# Revit family: Casement_36_B_Side_Hung_Standard
name_source: partatom
category: Windows
revit_build: Autodesk Revit 2014 (Build: 20130308_1515(x64)
units: mm (PartAtom-declared; Revit-internal decimal feet)

## types (18) — shared parameters
Aluminium Thickness = 1 mm  [stored 0.00328084 ft]
Bead SG Gap = 13 mm  [stored 0.0426509 ft]
Casement Dimension = 36 mm  [stored 0.11811 ft]
Custom Sash Width = 554 mm  [stored 1.81759 ft]
DG Extrusion Start = 8 mm  [stored 0.0262467 ft]
DG Gasket Finish = Double Glazing Gasket Material
DG Thickness Calc = 4 mm  [stored 0.0131234 ft]
Default Sill Height = 800 mm  [stored 2.62467 ft]
Depth Bead = 22 mm  [stored 0.0721785 ft]
Depth Mullion = 37 mm  [stored 0.121391 ft]
Description = Window 36mm, Type B side hung
Frame Center Offset = 18 mm  [stored 0.0590551 ft]
Limit Fixed Panel Width Max = 1500 mm
Limit Fixed Panel Width Min = 200 mm  [stored 0.656168 ft]
Limit Sash Height Max = 1300 mm  [stored 4.26509 ft]
Limit Sash Height Min = 300 mm  [stored 0.984252 ft]
Limit Sash Width Max = 600 mm  [stored 1.9685 ft]
Limit Sash Width Min = 300 mm  [stored 0.984252 ft]
Limit Window Height Max = 1346 mm  [stored 4.41601 ft]
Limit Window Height Min = 346 mm
Limit Window Width Max = 2129 mm
Limit Window Width Min = 829 mm  [stored 2.71982 ft]
Manufacturer = Crealco
Max System DG One Piece Thickness = 6 mm  [stored 0.019685 ft]
Max System DG Unit Thickness = 25 mm  [stored 0.082021 ft]
Model = Casement 36
Mullion Depth Windload Based = 37 mm  [stored 0.121391 ft]
Offset Bead SG Center Reversed = 18 mm  [stored 0.0590551 ft]
Offset Mullion Left = 569 mm  [stored 1.8668 ft]
Offset Panel 4 Left = 599 mm  [stored 1.96522 ft]
Offset Sash Left = 23 mm  [stored 0.0754593 ft]
Offset Sash Top = 23 mm  [stored 0.0754593 ft]
Offset Window Exterior = 18 mm  [stored 0.0590551 ft]
SG Gasket Thickness = 6 mm  [stored 0.019685 ft]
Sash Center Offset = 15 mm  [stored 0.0492126 ft]
Sash Overlap = 7 mm  [stored 0.0229659 ft]
Sash Spacing Inner = 8 mm  [stored 0.0262467 ft]
URL = http://www.crealco.co.za
Wall Closure = By host
Width Bead = 15 mm  [stored 0.0492126 ft]
Width Panel 1 = 539 mm  [stored 1.76837 ft]
Width Profile = 30 mm  [stored 0.0984252 ft]
Width Sash = 524 mm  [stored 1.71916 ft]
Width Sash Opening = 554 mm  [stored 1.81759 ft]
zero-valued in all types: Window Exterior Offset

## per-type parameters (varying)
- 36-0909S-1000Pa: Area Pane Left=0.37 m²; Area Pane Right=0.21 m²; Clearvue Insulated LowE SHGC Value=0.451; Clearvue Insulated LowE U Value=3.84; Clearvue Insulated SHGC Value=0.495; Clearvue Insulated U Value=4.31; Clearvue U Value=6.23; Custom Windload=1000 mm  [stored 3.28084 ft]; Custom Window Height=890 mm  [stored 2.91995 ft]; Custom Window Width=890 mm  [stored 2.91995 ft]; Energy Advantage SHGC Value=0.503; Energy Advantage U Value=4.91; Height=890 mm  [stored 2.91995 ft]; Height Panel 4=830 mm  [stored 2.7231 ft]; Height Sash=814 mm  [stored 2.6706 ft]; Height Sash Opening=844 mm  [stored 2.76903 ft]; Intruderprufe Insulated LowE SHGC Value=0.416; Intruderprufe Insulated LowE U Value=3.76; Intruderprufe Insulated SHGC Value=0.452; Intruderprufe Insulated U Value=4.19; Intruderprufe LowE SHGC Value=0.474; Intruderprufe LowE U Value=4.8; Intruderprufe SHGC Value=0.535; Intruderprufe U Value=6.09; Length Mullion=890 mm  [stored 2.91995 ft]; Max Pane Area=0.37 m²; Width=890 mm  [stored 2.91995 ft]; Width Panel 4=261 mm  [stored 0.856299 ft]; Windload Design=1000 mm  [stored 3.28084 ft]
- 36-1209S-1000Pa: Area Pane Left=0.37 m²; Area Pane Right=0.45 m²; Clearvue Insulated LowE SHGC Value=0.49; Clearvue Insulated LowE U Value=3.52; Clearvue Insulated SHGC Value=0.538; Clearvue Insulated U Value=4.04; Clearvue U Value=6.16; Custom Windload=1000 mm  [stored 3.28084 ft]; Custom Window Height=890 mm  [stored 2.91995 ft]; Custom Window Width=1190 mm  [stored 3.9042 ft]; Energy Advantage SHGC Value=0.546; Energy Advantage U Value=4.7; Height=890 mm  [stored 2.91995 ft]; Height Panel 4=830 mm  [stored 2.7231 ft]; Height Sash=814 mm  [stored 2.6706 ft]; Height Sash Opening=844 mm  [stored 2.76903 ft]; Intruderprufe Insulated LowE SHGC Value=0.451; Intruderprufe Insulated LowE U Value=3.44; Intruderprufe Insulated SHGC Value=0.492; Intruderprufe Insulated U Value=3.93; Intruderprufe LowE SHGC Value=0.513; Intruderprufe LowE U Value=4.59; Intruderprufe SHGC Value=0.581; Intruderprufe U Value=6.03; Length Mullion=890 mm  [stored 2.91995 ft]; Max Pane Area=0.45 m²; Width=1190 mm  [stored 3.9042 ft]; Width Panel 4=561 mm; Windload Design=1000 mm  [stored 3.28084 ft]
- 36-1509S-1000Pa: Area Pane Left=0.37 m²; Area Pane Right=0.7 m²; Clearvue Insulated LowE SHGC Value=0.513; Clearvue Insulated LowE U Value=3.32; Clearvue Insulated SHGC Value=0.563; Clearvue Insulated U Value=3.87; Clearvue U Value=6.12; Custom Windload=1000 mm  [stored 3.28084 ft]; Custom Window Height=890 mm  [stored 2.91995 ft]; Custom Window Width=1490 mm; Energy Advantage SHGC Value=0.572; Energy Advantage U Value=4.58; Height=890 mm  [stored 2.91995 ft]; Height Panel 4=830 mm  [stored 2.7231 ft]; Height Sash=814 mm  [stored 2.6706 ft]; Height Sash Opening=844 mm  [stored 2.76903 ft]; Intruderprufe Insulated LowE SHGC Value=0.472; Intruderprufe Insulated LowE U Value=3.25; Intruderprufe Insulated SHGC Value=0.516; Intruderprufe Insulated U Value=3.78; Intruderprufe LowE SHGC Value=0.537; Intruderprufe LowE U Value=4.47; Intruderprufe SHGC Value=0.609; Intruderprufe U Value=5.99; Length Mullion=890 mm  [stored 2.91995 ft]; Max Pane Area=0.7 m²; Width=1490 mm; Width Panel 4=861 mm  [stored 2.8248 ft]; Windload Design=1000 mm  [stored 3.28084 ft]
- 36-0912S-1000Pa: Area Pane Left=0.52 m²; Area Pane Right=0.28 m²; Clearvue Insulated LowE SHGC Value=0.469; Clearvue Insulated LowE U Value=3.71; Clearvue Insulated SHGC Value=0.515; Clearvue Insulated U Value=4.19; Clearvue U Value=6.21; Custom Windload=1000 mm  [stored 3.28084 ft]; Custom Window Height=1190 mm  [stored 3.9042 ft]; Custom Window Width=890 mm  [stored 2.91995 ft]; Energy Advantage SHGC Value=0.523; Energy Advantage U Value=4.82; Height=1190 mm  [stored 3.9042 ft]; Height Panel 4=1130 mm  [stored 3.70735 ft]; Height Sash=1114 mm  [stored 3.65486 ft]; Height Sash Opening=1144 mm; Intruderprufe Insulated LowE SHGC Value=0.432; Intruderprufe Insulated LowE U Value=3.62; Intruderprufe Insulated SHGC Value=0.471; Intruderprufe Insulated U Value=4.08; Intruderprufe LowE SHGC Value=0.493; Intruderprufe LowE U Value=4.71; Intruderprufe SHGC Value=0.556; Intruderprufe U Value=6.07; Length Mullion=1190 mm  [stored 3.9042 ft]; Max Pane Area=0.52 m²; Width=890 mm  [stored 2.91995 ft]; Width Panel 4=261 mm  [stored 0.856299 ft]; Windload Design=1000 mm  [stored 3.28084 ft]
- 36-1212S-1000Pa: Area Pane Left=0.52 m²; Area Pane Right=0.62 m²; Clearvue Insulated LowE SHGC Value=0.508; Clearvue Insulated LowE U Value=3.37; Clearvue Insulated SHGC Value=0.558; Clearvue Insulated U Value=3.92; Clearvue U Value=6.14; Custom Windload=1000 mm  [stored 3.28084 ft]; Custom Window Height=1190 mm  [stored 3.9042 ft]; Custom Window Width=1190 mm  [stored 3.9042 ft]; Energy Advantage SHGC Value=0.567; Energy Advantage U Value=4.61; Height=1190 mm  [stored 3.9042 ft]; Height Panel 4=1130 mm  [stored 3.70735 ft]; Height Sash=1114 mm  [stored 3.65486 ft]; Height Sash Opening=1144 mm; Intruderprufe Insulated LowE SHGC Value=0.469; Intruderprufe Insulated LowE U Value=3.3; Intruderprufe Insulated SHGC Value=0.511; Intruderprufe Insulated U Value=3.82; Intruderprufe LowE SHGC Value=0.532; Intruderprufe LowE U Value=4.51; Intruderprufe SHGC Value=0.603; Intruderprufe U Value=6; Length Mullion=1190 mm  [stored 3.9042 ft]; Max Pane Area=0.62 m²; Width=1190 mm  [stored 3.9042 ft]; Width Panel 4=561 mm; Windload Design=1000 mm  [stored 3.28084 ft]
- 36-1512S-1000Pa: Area Pane Left=0.52 m²; Area Pane Right=0.95 m²; Clearvue Insulated LowE SHGC Value=0.531; Clearvue Insulated LowE U Value=3.17; Clearvue Insulated SHGC Value=0.584; Clearvue Insulated U Value=3.75; Clearvue U Value=6.1; Custom Windload=1000 mm  [stored 3.28084 ft]; Custom Window Height=1190 mm  [stored 3.9042 ft]; Custom Window Width=1490 mm; Energy Advantage SHGC Value=0.593; Energy Advantage U Value=4.49; Height=1190 mm  [stored 3.9042 ft]; Height Panel 4=1130 mm  [stored 3.70735 ft]; Height Sash=1114 mm  [stored 3.65486 ft]; Height Sash Opening=1144 mm; Intruderprufe Insulated LowE SHGC Value=0.489; Intruderprufe Insulated LowE U Value=3.1; Intruderprufe Insulated SHGC Value=0.536; Intruderprufe Insulated U Value=3.66; Intruderprufe LowE SHGC Value=0.556; Intruderprufe LowE U Value=4.38; Intruderprufe SHGC Value=0.63; Intruderprufe U Value=5.96; Length Mullion=1190 mm  [stored 3.9042 ft]; Max Pane Area=0.95 m²; Width=1490 mm; Width Panel 4=861 mm  [stored 2.8248 ft]; Windload Design=1000 mm  [stored 3.28084 ft]
- 36-0909S-1500Pa: Area Pane Left=0.37 m²; Area Pane Right=0.21 m²; Clearvue Insulated LowE SHGC Value=0.451; Clearvue Insulated LowE U Value=3.84; Clearvue Insulated SHGC Value=0.495; Clearvue Insulated U Value=4.31; Clearvue U Value=6.23; Custom Windload=1500 mm; Custom Window Height=890 mm  [stored 2.91995 ft]; Custom Window Width=890 mm  [stored 2.91995 ft]; Energy Advantage SHGC Value=0.503; Energy Advantage U Value=4.91; Height=890 mm  [stored 2.91995 ft]; Height Panel 4=830 mm  [stored 2.7231 ft]; Height Sash=814 mm  [stored 2.6706 ft]; Height Sash Opening=844 mm  [stored 2.76903 ft]; Intruderprufe Insulated LowE SHGC Value=0.416; Intruderprufe Insulated LowE U Value=3.76; Intruderprufe Insulated SHGC Value=0.452; Intruderprufe Insulated U Value=4.19; Intruderprufe LowE SHGC Value=0.474; Intruderprufe LowE U Value=4.8; Intruderprufe SHGC Value=0.535; Intruderprufe U Value=6.09; Length Mullion=890 mm  [stored 2.91995 ft]; Max Pane Area=0.37 m²; Width=890 mm  [stored 2.91995 ft]; Width Panel 4=261 mm  [stored 0.856299 ft]; Windload Design=1500 mm
- 36-0909S-2000Pa: Area Pane Left=0.37 m²; Area Pane Right=0.21 m²; Clearvue Insulated LowE SHGC Value=0.451; Clearvue Insulated LowE U Value=3.84; Clearvue Insulated SHGC Value=0.495; Clearvue Insulated U Value=4.31; Clearvue U Value=6.23; Custom Windload=2000 mm; Custom Window Height=890 mm  [stored 2.91995 ft]; Custom Window Width=890 mm  [stored 2.91995 ft]; Energy Advantage SHGC Value=0.503; Energy Advantage U Value=4.91; Height=890 mm  [stored 2.91995 ft]; Height Panel 4=830 mm  [stored 2.7231 ft]; Height Sash=814 mm  [stored 2.6706 ft]; Height Sash Opening=844 mm  [stored 2.76903 ft]; Intruderprufe Insulated LowE SHGC Value=0.416; Intruderprufe Insulated LowE U Value=3.76; Intruderprufe Insulated SHGC Value=0.452; Intruderprufe Insulated U Value=4.19; Intruderprufe LowE SHGC Value=0.474; Intruderprufe LowE U Value=4.8; Intruderprufe SHGC Value=0.535; Intruderprufe U Value=6.09; Length Mullion=890 mm  [stored 2.91995 ft]; Max Pane Area=0.37 m²; Width=890 mm  [stored 2.91995 ft]; Width Panel 4=261 mm  [stored 0.856299 ft]; Windload Design=2000 mm
- 36-1209S-1500Pa: Area Pane Left=0.37 m²; Area Pane Right=0.45 m²; Clearvue Insulated LowE SHGC Value=0.49; Clearvue Insulated LowE U Value=3.52; Clearvue Insulated SHGC Value=0.538; Clearvue Insulated U Value=4.04; Clearvue U Value=6.16; Custom Windload=1500 mm; Custom Window Height=890 mm  [stored 2.91995 ft]; Custom Window Width=1190 mm  [stored 3.9042 ft]; Energy Advantage SHGC Value=0.546; Energy Advantage U Value=4.7; Height=890 mm  [stored 2.91995 ft]; Height Panel 4=830 mm  [stored 2.7231 ft]; Height Sash=814 mm  [stored 2.6706 ft]; Height Sash Opening=844 mm  [stored 2.76903 ft]; Intruderprufe Insulated LowE SHGC Value=0.451; Intruderprufe Insulated LowE U Value=3.44; Intruderprufe Insulated SHGC Value=0.492; Intruderprufe Insulated U Value=3.93; Intruderprufe LowE SHGC Value=0.513; Intruderprufe LowE U Value=4.59; Intruderprufe SHGC Value=0.581; Intruderprufe U Value=6.03; Length Mullion=890 mm  [stored 2.91995 ft]; Max Pane Area=0.45 m²; Width=1190 mm  [stored 3.9042 ft]; Width Panel 4=561 mm; Windload Design=1500 mm
- 36-1209S-2000Pa: Area Pane Left=0.37 m²; Area Pane Right=0.45 m²; Clearvue Insulated LowE SHGC Value=0.49; Clearvue Insulated LowE U Value=3.52; Clearvue Insulated SHGC Value=0.538; Clearvue Insulated U Value=4.04; Clearvue U Value=6.16; Custom Windload=2000 mm; Custom Window Height=890 mm  [stored 2.91995 ft]; Custom Window Width=1190 mm  [stored 3.9042 ft]; Energy Advantage SHGC Value=0.546; Energy Advantage U Value=4.7; Height=890 mm  [stored 2.91995 ft]; Height Panel 4=830 mm  [stored 2.7231 ft]; Height Sash=814 mm  [stored 2.6706 ft]; Height Sash Opening=844 mm  [stored 2.76903 ft]; Intruderprufe Insulated LowE SHGC Value=0.451; Intruderprufe Insulated LowE U Value=3.44; Intruderprufe Insulated SHGC Value=0.492; Intruderprufe Insulated U Value=3.93; Intruderprufe LowE SHGC Value=0.513; Intruderprufe LowE U Value=4.59; Intruderprufe SHGC Value=0.581; Intruderprufe U Value=6.03; Length Mullion=890 mm  [stored 2.91995 ft]; Max Pane Area=0.45 m²; Width=1190 mm  [stored 3.9042 ft]; Width Panel 4=561 mm; Windload Design=2000 mm
- 36-1509S-1500Pa: Area Pane Left=0.37 m²; Area Pane Right=0.7 m²; Clearvue Insulated LowE SHGC Value=0.513; Clearvue Insulated LowE U Value=3.32; Clearvue Insulated SHGC Value=0.563; Clearvue Insulated U Value=3.87; Clearvue U Value=6.12; Custom Windload=1500 mm; Custom Window Height=890 mm  [stored 2.91995 ft]; Custom Window Width=1490 mm; Energy Advantage SHGC Value=0.572; Energy Advantage U Value=4.58; Height=890 mm  [stored 2.91995 ft]; Height Panel 4=830 mm  [stored 2.7231 ft]; Height Sash=814 mm  [stored 2.6706 ft]; Height Sash Opening=844 mm  [stored 2.76903 ft]; Intruderprufe Insulated LowE SHGC Value=0.472; Intruderprufe Insulated LowE U Value=3.25; Intruderprufe Insulated SHGC Value=0.516; Intruderprufe Insulated U Value=3.78; Intruderprufe LowE SHGC Value=0.537; Intruderprufe LowE U Value=4.47; Intruderprufe SHGC Value=0.609; Intruderprufe U Value=5.99; Length Mullion=890 mm  [stored 2.91995 ft]; Max Pane Area=0.7 m²; Width=1490 mm; Width Panel 4=861 mm  [stored 2.8248 ft]; Windload Design=1500 mm
- 36-1509S-2000Pa: Area Pane Left=0.37 m²; Area Pane Right=0.7 m²; Clearvue Insulated LowE SHGC Value=0.513; Clearvue Insulated LowE U Value=3.32; Clearvue Insulated SHGC Value=0.563; Clearvue Insulated U Value=3.87; Clearvue U Value=6.12; Custom Windload=2000 mm; Custom Window Height=890 mm  [stored 2.91995 ft]; Custom Window Width=1490 mm; Energy Advantage SHGC Value=0.572; Energy Advantage U Value=4.58; Height=890 mm  [stored 2.91995 ft]; Height Panel 4=830 mm  [stored 2.7231 ft]; Height Sash=814 mm  [stored 2.6706 ft]; Height Sash Opening=844 mm  [stored 2.76903 ft]; Intruderprufe Insulated LowE SHGC Value=0.472; Intruderprufe Insulated LowE U Value=3.25; Intruderprufe Insulated SHGC Value=0.516; Intruderprufe Insulated U Value=3.78; Intruderprufe LowE SHGC Value=0.537; Intruderprufe LowE U Value=4.47; Intruderprufe SHGC Value=0.609; Intruderprufe U Value=5.99; Length Mullion=890 mm  [stored 2.91995 ft]; Max Pane Area=0.7 m²; Width=1490 mm; Width Panel 4=861 mm  [stored 2.8248 ft]; Windload Design=2000 mm
- 36-0912S-1500Pa: Area Pane Left=0.52 m²; Area Pane Right=0.28 m²; Clearvue Insulated LowE SHGC Value=0.469; Clearvue Insulated LowE U Value=3.71; Clearvue Insulated SHGC Value=0.515; Clearvue Insulated U Value=4.19; Clearvue U Value=6.21; Custom Windload=1500 mm; Custom Window Height=1190 mm  [stored 3.9042 ft]; Custom Window Width=890 mm  [stored 2.91995 ft]; Energy Advantage SHGC Value=0.523; Energy Advantage U Value=4.82; Height=1190 mm  [stored 3.9042 ft]; Height Panel 4=1130 mm  [stored 3.70735 ft]; Height Sash=1114 mm  [stored 3.65486 ft]; Height Sash Opening=1144 mm; Intruderprufe Insulated LowE SHGC Value=0.432; Intruderprufe Insulated LowE U Value=3.62; Intruderprufe Insulated SHGC Value=0.471; Intruderprufe Insulated U Value=4.08; Intruderprufe LowE SHGC Value=0.493; Intruderprufe LowE U Value=4.71; Intruderprufe SHGC Value=0.556; Intruderprufe U Value=6.07; Length Mullion=1190 mm  [stored 3.9042 ft]; Max Pane Area=0.52 m²; Width=890 mm  [stored 2.91995 ft]; Width Panel 4=261 mm  [stored 0.856299 ft]; Windload Design=1500 mm
- 36-0912S-2000Pa: Area Pane Left=0.52 m²; Area Pane Right=0.28 m²; Clearvue Insulated LowE SHGC Value=0.469; Clearvue Insulated LowE U Value=3.71; Clearvue Insulated SHGC Value=0.515; Clearvue Insulated U Value=4.19; Clearvue U Value=6.21; Custom Windload=2000 mm; Custom Window Height=1190 mm  [stored 3.9042 ft]; Custom Window Width=890 mm  [stored 2.91995 ft]; Energy Advantage SHGC Value=0.523; Energy Advantage U Value=4.82; Height=1190 mm  [stored 3.9042 ft]; Height Panel 4=1130 mm  [stored 3.70735 ft]; Height Sash=1114 mm  [stored 3.65486 ft]; Height Sash Opening=1144 mm; Intruderprufe Insulated LowE SHGC Value=0.432; Intruderprufe Insulated LowE U Value=3.62; Intruderprufe Insulated SHGC Value=0.471; Intruderprufe Insulated U Value=4.08; Intruderprufe LowE SHGC Value=0.493; Intruderprufe LowE U Value=4.71; Intruderprufe SHGC Value=0.556; Intruderprufe U Value=6.07; Length Mullion=1190 mm  [stored 3.9042 ft]; Max Pane Area=0.52 m²; Width=890 mm  [stored 2.91995 ft]; Width Panel 4=261 mm  [stored 0.856299 ft]; Windload Design=2000 mm
- 36-1212S-1500Pa: Area Pane Left=0.52 m²; Area Pane Right=0.62 m²; Clearvue Insulated LowE SHGC Value=0.508; Clearvue Insulated LowE U Value=3.37; Clearvue Insulated SHGC Value=0.558; Clearvue Insulated U Value=3.92; Clearvue U Value=6.14; Custom Windload=1500 mm; Custom Window Height=1190 mm  [stored 3.9042 ft]; Custom Window Width=1190 mm  [stored 3.9042 ft]; Energy Advantage SHGC Value=0.567; Energy Advantage U Value=4.61; Height=1190 mm  [stored 3.9042 ft]; Height Panel 4=1130 mm  [stored 3.70735 ft]; Height Sash=1114 mm  [stored 3.65486 ft]; Height Sash Opening=1144 mm; Intruderprufe Insulated LowE SHGC Value=0.469; Intruderprufe Insulated LowE U Value=3.3; Intruderprufe Insulated SHGC Value=0.511; Intruderprufe Insulated U Value=3.82; Intruderprufe LowE SHGC Value=0.532; Intruderprufe LowE U Value=4.51; Intruderprufe SHGC Value=0.603; Intruderprufe U Value=6; Length Mullion=1190 mm  [stored 3.9042 ft]; Max Pane Area=0.62 m²; Width=1190 mm  [stored 3.9042 ft]; Width Panel 4=561 mm; Windload Design=1500 mm
- 36-1212S-2000Pa: Area Pane Left=0.52 m²; Area Pane Right=0.62 m²; Clearvue Insulated LowE SHGC Value=0.508; Clearvue Insulated LowE U Value=3.37; Clearvue Insulated SHGC Value=0.558; Clearvue Insulated U Value=3.92; Clearvue U Value=6.14; Custom Windload=2000 mm; Custom Window Height=1190 mm  [stored 3.9042 ft]; Custom Window Width=1190 mm  [stored 3.9042 ft]; Energy Advantage SHGC Value=0.567; Energy Advantage U Value=4.61; Height=1190 mm  [stored 3.9042 ft]; Height Panel 4=1130 mm  [stored 3.70735 ft]; Height Sash=1114 mm  [stored 3.65486 ft]; Height Sash Opening=1144 mm; Intruderprufe Insulated LowE SHGC Value=0.469; Intruderprufe Insulated LowE U Value=3.3; Intruderprufe Insulated SHGC Value=0.511; Intruderprufe Insulated U Value=3.82; Intruderprufe LowE SHGC Value=0.532; Intruderprufe LowE U Value=4.51; Intruderprufe SHGC Value=0.603; Intruderprufe U Value=6; Length Mullion=1190 mm  [stored 3.9042 ft]; Max Pane Area=0.62 m²; Width=1190 mm  [stored 3.9042 ft]; Width Panel 4=561 mm; Windload Design=2000 mm
- 36-1512S-1500Pa: Area Pane Left=0.52 m²; Area Pane Right=0.95 m²; Clearvue Insulated LowE SHGC Value=0.531; Clearvue Insulated LowE U Value=3.17; Clearvue Insulated SHGC Value=0.584; Clearvue Insulated U Value=3.75; Clearvue U Value=6.1; Custom Windload=1500 mm; Custom Window Height=1190 mm  [stored 3.9042 ft]; Custom Window Width=1490 mm; Energy Advantage SHGC Value=0.593; Energy Advantage U Value=4.49; Height=1190 mm  [stored 3.9042 ft]; Height Panel 4=1130 mm  [stored 3.70735 ft]; Height Sash=1114 mm  [stored 3.65486 ft]; Height Sash Opening=1144 mm; Intruderprufe Insulated LowE SHGC Value=0.489; Intruderprufe Insulated LowE U Value=3.1; Intruderprufe Insulated SHGC Value=0.536; Intruderprufe Insulated U Value=3.66; Intruderprufe LowE SHGC Value=0.556; Intruderprufe LowE U Value=4.38; Intruderprufe SHGC Value=0.63; Intruderprufe U Value=5.96; Length Mullion=1190 mm  [stored 3.9042 ft]; Max Pane Area=0.95 m²; Width=1490 mm; Width Panel 4=861 mm  [stored 2.8248 ft]; Windload Design=1500 mm
- 36-1512S-2000Pa: Area Pane Left=0.52 m²; Area Pane Right=0.95 m²; Clearvue Insulated LowE SHGC Value=0.531; Clearvue Insulated LowE U Value=3.17; Clearvue Insulated SHGC Value=0.584; Clearvue Insulated U Value=3.75; Clearvue U Value=6.1; Custom Windload=2000 mm; Custom Window Height=1190 mm  [stored 3.9042 ft]; Custom Window Width=1490 mm; Energy Advantage SHGC Value=0.593; Energy Advantage U Value=4.49; Height=1190 mm  [stored 3.9042 ft]; Height Panel 4=1130 mm  [stored 3.70735 ft]; Height Sash=1114 mm  [stored 3.65486 ft]; Height Sash Opening=1144 mm; Intruderprufe Insulated LowE SHGC Value=0.489; Intruderprufe Insulated LowE U Value=3.1; Intruderprufe Insulated SHGC Value=0.536; Intruderprufe Insulated U Value=3.66; Intruderprufe LowE SHGC Value=0.556; Intruderprufe LowE U Value=4.38; Intruderprufe SHGC Value=0.63; Intruderprufe U Value=5.96; Length Mullion=1190 mm  [stored 3.9042 ft]; Max Pane Area=0.95 m²; Width=1490 mm; Width Panel 4=861 mm  [stored 2.8248 ft]; Windload Design=2000 mm

note: [stored X ft] marks values corroborated as IEEE doubles in the binary element streams (Revit-internal decimal feet)

## geometry (parser evidence)
native form markers: Extrusion x1, Sweep x28
no freeform markers — native parametric forms only
